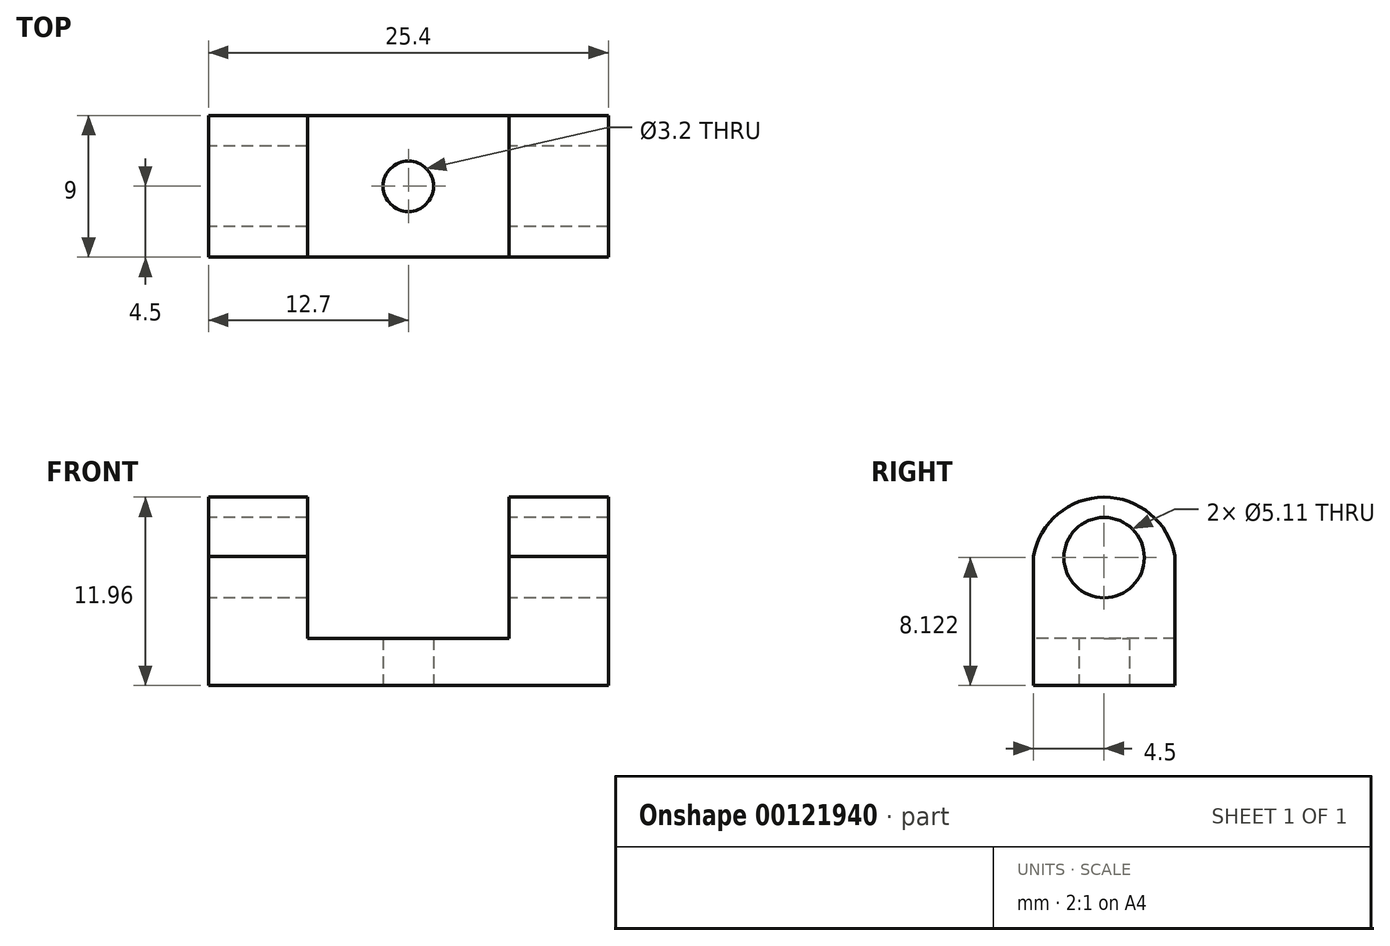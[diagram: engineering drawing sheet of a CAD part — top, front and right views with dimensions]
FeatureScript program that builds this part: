
annotation { "Feature Type Name" : "Feature", "Feature Type Description" : "" }
export const myFeature = defineFeature(function(context is Context, id is Id, definition is map)
    precondition{}
    {
        {
            var Q0;
            Q0=qCreatedBy(makeId("Top.planeOp"),FACE);
            var sketch = newSketch(context, id + "F0", { "sketchPlane" : qUnion([Q0])});
            skLineSegment(sketch, "E0.bottom", {"start": v(-12.7, 4.5) * mm, "end": v(12.7, 4.5) * mm});
            skLineSegment(sketch, "E0.top", {"start": v(-12.7, -4.5) * mm, "end": v(12.7, -4.5) * mm});
            skLineSegment(sketch, "E0.left", {"start": v(-12.7, 4.5) * mm, "end": v(-12.7, -4.5) * mm});
            skLineSegment(sketch, "E0.right", {"start": v(12.7, 4.5) * mm, "end": v(12.7, -4.5) * mm});
            skPoint(sketch, "E0.middle", {"position": v(0, 0) * mm});
            skSolve(sketch);
        }
        {
            var Q0;
            Q0=makeQuery(id+"F0.imprint","IMPRINT",FACE,{"disambiguationData":[TD([[makeQuery(id+"F0.imprint","IMPRINT",EDGE,{"derivedFrom":sQuery(id+"F0.wireOp",EDGE,"E0.bottom")}),-1.0]])]});
            extrude(context, id + "F1", {"entities" : qUnion([Q0]), "depth" : 3 * mm});
        }
        {
            var Q0;
            Q0=makeQuery(id+"F1.opExtrude","CAP_FACE",FACE,{"disambiguationData":[OSD([sQuery(id+"F0.wireOp",EDGE,"E0.bottom"),sQuery(id+"F0.wireOp",EDGE,"E0.top"),sQuery(id+"F0.wireOp",EDGE,"E0.left"),sQuery(id+"F0.wireOp",EDGE,"E0.right")])],"isStart":false});
            var sketch = newSketch(context, id + "F2", { "sketchPlane" : qUnion([Q0])});
            skLineSegment(sketch, "E1.bottom", {"start": v(-12.7, 4.5) * mm, "end": v(-6.4, 4.5) * mm});
            skLineSegment(sketch, "E1.top", {"start": v(-12.7, -4.5) * mm, "end": v(-6.4, -4.5) * mm});
            skLineSegment(sketch, "E1.left", {"start": v(-12.7, 4.5) * mm, "end": v(-12.7, -4.5) * mm});
            skLineSegment(sketch, "E1.right", {"start": v(-6.4, 4.5) * mm, "end": v(-6.4, -4.5) * mm});
            skLineSegment(sketch, "E2.bottom", {"start": v(12.7, 4.5) * mm, "end": v(6.4, 4.5) * mm});
            skLineSegment(sketch, "E2.top", {"start": v(12.7, -4.5) * mm, "end": v(6.4, -4.5) * mm});
            skLineSegment(sketch, "E2.left", {"start": v(12.7, 4.5) * mm, "end": v(12.7, -4.5) * mm});
            skLineSegment(sketch, "E2.right", {"start": v(6.4, 4.5) * mm, "end": v(6.4, -4.5) * mm});
            skSolve(sketch);
        }
        {
            var Q0;
            Q0 = qSketchRegion(id + "F2", true);
            extrude(context, id + "F3", {"entities" : qUnion([Q0]), "operationType" : NewBodyOperationType.ADD, "depth" : 9 * mm});
        }
        {
            var Q0;
            Q0=makeQuery(id+"F3.boolean.opBoolean","MERGE",FACE,{"derivedFrom":[makeQuery(id+"F1.opExtrude","SWEPT_FACE",FACE,{"disambiguationData":[OSD([sQuery(id+"F0.wireOp",EDGE,"E0.right")])]}),makeQuery(id+"F3.opExtrude","SWEPT_FACE",FACE,{"disambiguationData":[OSD([sQuery(id+"F2.wireOp",EDGE,"E2.left")])]})]});
            var sketch = newSketch(context, id + "F4", { "sketchPlane" : qUnion([Q0])});
            skArc(sketch, "E3", {"start": v(4.5, 8.23) * mm, "mid": v(-0.01, 11.96) * mm, "end": v(-4.5, 8.2) * mm});
            skSolve(sketch);
        }
        {
            var Q0;
            {var subQ0=sQuery(id+"F4.wireOp",EDGE,"E3");Q0=makeQuery(id+"F4.imprint","IMPRINT",FACE,{"disambiguationData":[TD([[makeQuery(id+"F4.imprint","IMPRINT",EDGE,{"derivedFrom":subQ0}),-1.0]])]});}
            extrude(context, id + "F5", {"entities" : qUnion([Q0]), "operationType" : NewBodyOperationType.REMOVE, "oppositeDirection" : true, "depth" : 25 * mm});
        }
        {
            var Q0;
            Q0=makeQuery(id+"F5.boolean.opBoolean","COPY",FACE,{"derivedFrom":makeQuery(id+"F5.opExtrude","CAP_FACE",FACE,{"disambiguationData":[OSD([sQuery(id+"F0.wireOp",EDGE,"E0.bottom"),sQuery(id+"F0.wireOp",EDGE,"E0.top"),sQuery(id+"F0.wireOp",EDGE,"E0.right"),sQuery(id+"F2.wireOp",EDGE,"E2.bottom"),sQuery(id+"F2.wireOp",EDGE,"E2.top"),sQuery(id+"F2.wireOp",EDGE,"E2.left"),sQuery(id+"F4.wireOp",EDGE,"E3")])],"isStart":false})});
            extrude(context, id + "F6", {"entities" : qUnion([Q0]), "operationType" : NewBodyOperationType.REMOVE, "oppositeDirection" : true, "depth" : 25 * mm});
        }
        {
            var Q0;
            Q0=makeQuery(id+"F3.boolean.opBoolean","MERGE",FACE,{"derivedFrom":[makeQuery(id+"F1.opExtrude","SWEPT_FACE",FACE,{"disambiguationData":[OSD([sQuery(id+"F0.wireOp",EDGE,"E0.left")])]}),makeQuery(id+"F3.opExtrude","SWEPT_FACE",FACE,{"disambiguationData":[OSD([sQuery(id+"F2.wireOp",EDGE,"E1.left")])]})]});
            var sketch = newSketch(context, id + "F7", { "sketchPlane" : qUnion([Q0])});
            skPoint(sketch, "E4", {"position": v(0, 8.12) * mm});
            skSolve(sketch);
        }
        {
            var Q0;
            Q0=sQuery(id+"F7.wireOp",VERTEX,"E4");
            var Q1;
            Q1=makeQuery(id+"F1.opExtrude","SWEPT_BODY",BODY,{"disambiguationData":[OSD([sQuery(id+"F0.wireOp",EDGE,"E0.bottom"),sQuery(id+"F0.wireOp",EDGE,"E0.top"),sQuery(id+"F0.wireOp",EDGE,"E0.left"),sQuery(id+"F0.wireOp",EDGE,"E0.right")])]});
            hole(context, id + "F8", {"style" : HoleStyle.SIMPLE, "endStyle" : HoleEndStyle.THROUGH, "standardTappedOrClearance" : lookupTablePath({ "standard" : "ANSI", "fit" : "Normal (ASME)", "size" : "#10", "type" : "Clearance" }), "standardBlindInLast" : lookupTablePath({ "fit" : "Free", "standard" : "ANSI", "size" : "#10", "type" : "Clearance" }), "holeDiameter" : 5.1 * mm, "locations" : qUnion([Q0]), "scope" : qUnion([Q1]), "isTappedThrough" : true});
        }
        {
            var Q0;
            Q0=sQuery(id+"F0.wireOp",VERTEX,"E0.middle");
            var Q1;
            Q1=makeQuery(id+"F1.opExtrude","SWEPT_BODY",BODY,{"disambiguationData":[OSD([sQuery(id+"F0.wireOp",EDGE,"E0.bottom"),sQuery(id+"F0.wireOp",EDGE,"E0.top"),sQuery(id+"F0.wireOp",EDGE,"E0.left"),sQuery(id+"F0.wireOp",EDGE,"E0.right")])]});
            hole(context, id + "F9", {"style" : HoleStyle.SIMPLE, "endStyle" : HoleEndStyle.THROUGH, "oppositeDirection" : true, "holeDiameter" : 3.2 * mm, "locations" : qUnion([Q0]), "scope" : qUnion([Q1]), "isTappedThrough" : true});
        }
    });
